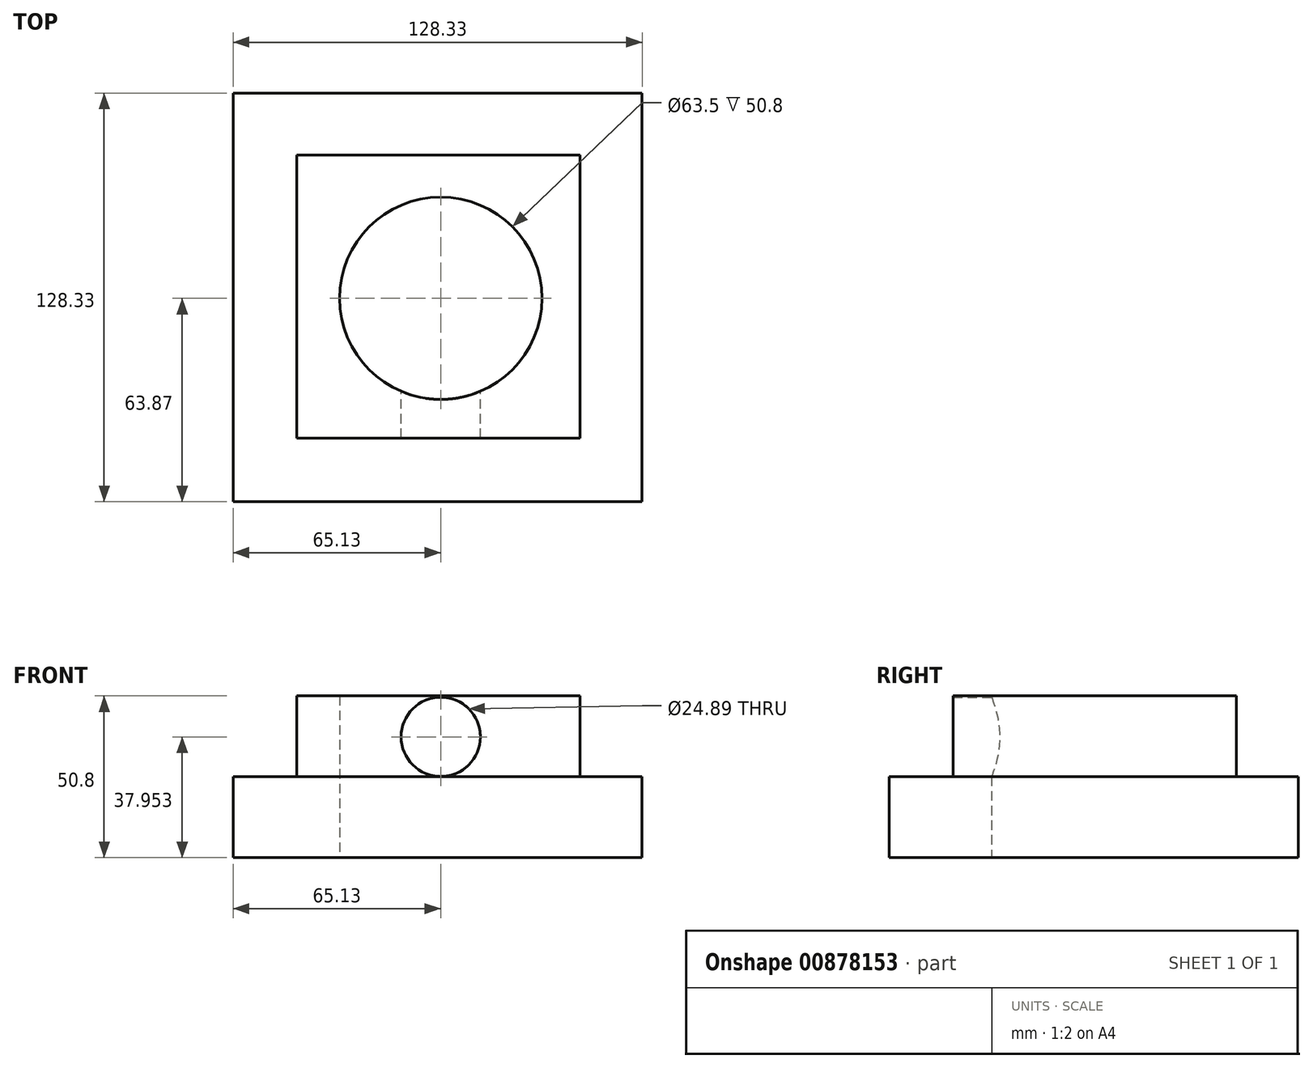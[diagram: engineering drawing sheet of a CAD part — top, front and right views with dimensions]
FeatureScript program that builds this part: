
annotation { "Feature Type Name" : "Feature", "Feature Type Description" : "" }
export const myFeature = defineFeature(function(context is Context, id is Id, definition is map)
    precondition{}
    {
        {
            var Q0;
            Q0=qCreatedBy(makeId("Top.planeOp"),FACE);
            var sketch = newSketch(context, id + "F0", { "sketchPlane" : qUnion([Q0])});
            skLineSegment(sketch, "E0.bottom", {"start": v(-65.13, 64.46) * mm, "end": v(63.2, 64.46) * mm});
            skLineSegment(sketch, "E0.top", {"start": v(-65.13, -63.87) * mm, "end": v(63.2, -63.87) * mm});
            skLineSegment(sketch, "E0.left", {"start": v(-65.13, 64.46) * mm, "end": v(-65.13, -63.87) * mm});
            skLineSegment(sketch, "E0.right", {"start": v(63.2, 64.46) * mm, "end": v(63.2, -63.87) * mm});
            skLineSegment(sketch, "E1.bottom", {"start": v(-45.15, 45.01) * mm, "end": v(43.75, 45.01) * mm});
            skLineSegment(sketch, "E1.top", {"start": v(-45.15, -43.89) * mm, "end": v(43.75, -43.89) * mm});
            skLineSegment(sketch, "E1.left", {"start": v(-45.15, 45.01) * mm, "end": v(-45.15, -43.89) * mm});
            skLineSegment(sketch, "E1.right", {"start": v(43.75, 45.01) * mm, "end": v(43.75, -43.89) * mm});
            skSolve(sketch);
        }
        {
            var Q0;
            Q0=makeQuery(id+"F0.imprint","IMPRINT",FACE,{"disambiguationData":[TD([[makeQuery(id+"F0.imprint","IMPRINT",EDGE,{"derivedFrom":sQuery(id+"F0.wireOp",EDGE,"E1.bottom")}),-1.0]])]});
            extrude(context, id + "F1", {"entities" : qUnion([Q0]), "depth" : 50.8 * mm, "offsetDistance" : 25.4 * mm});
        }
        {
            var Q0;
            Q0 = qSketchRegion(id + "F0", true);
            extrude(context, id + "F2", {"entities" : qUnion([Q0]), "operationType" : NewBodyOperationType.ADD, "depth" : 25.4 * mm, "offsetDistance" : 25.4 * mm});
        }
        {
            var Q0;
            Q0=qCreatedBy(makeId("Top.planeOp"),FACE);
            var sketch = newSketch(context, id + "F3", { "sketchPlane" : qUnion([Q0])});
            skCircle(sketch, "E2", {"center": v(0, 0) * mm, "radius": 31.75 * mm});
            skSolve(sketch);
        }
        {
            var Q0;
            Q0=sQuery(id+"F3.wireOp",VERTEX,"E2.center");
            var Q1;
            Q1=makeQuery(id+"F1.opExtrude","SWEPT_BODY",BODY,{"disambiguationData":[OSD([sQuery(id+"F0.wireOp",EDGE,"E1.bottom"),sQuery(id+"F0.wireOp",EDGE,"E1.top"),sQuery(id+"F0.wireOp",EDGE,"E1.left"),sQuery(id+"F0.wireOp",EDGE,"E1.right")])]});
            hole(context, id + "F4", {"style" : HoleStyle.SIMPLE, "endStyle" : HoleEndStyle.THROUGH, "oppositeDirection" : true, "holeDiameter" : 63.5 * mm, "majorDiameter" : 6.35 * mm, "isTappedThrough" : true, "tappedDepth" : 12.7 * mm, "tapClearance" : 3, "locations" : qUnion([Q0]), "scope" : qUnion([Q1])});
        }
        {
            var Q0;
            Q0=qCreatedBy(makeId("Front.planeOp"),FACE);
            var sketch = newSketch(context, id + "F5", { "sketchPlane" : qUnion([Q0])});
            skCircle(sketch, "E3", {"center": v(0, 37.95) * mm, "radius": 12.1 * mm});
            skSolve(sketch);
        }
        {
            var Q0;
            Q0=sQuery(id+"F5.wireOp",VERTEX,"E3.center");
            var Q1;
            Q1=makeQuery(id+"F1.opExtrude","SWEPT_BODY",BODY,{"disambiguationData":[OSD([sQuery(id+"F0.wireOp",EDGE,"E1.bottom"),sQuery(id+"F0.wireOp",EDGE,"E1.top"),sQuery(id+"F0.wireOp",EDGE,"E1.left"),sQuery(id+"F0.wireOp",EDGE,"E1.right")])]});
            hole(context, id + "F6", {"style" : HoleStyle.SIMPLE, "endStyle" : HoleEndStyle.THROUGH, "oppositeDirection" : true, "holeDiameter" : 24.9 * mm, "majorDiameter" : 6.35 * mm, "isTappedThrough" : true, "tappedDepth" : 12.7 * mm, "tapClearance" : 3, "locations" : qUnion([Q0]), "scope" : qUnion([Q1])});
        }
    });
